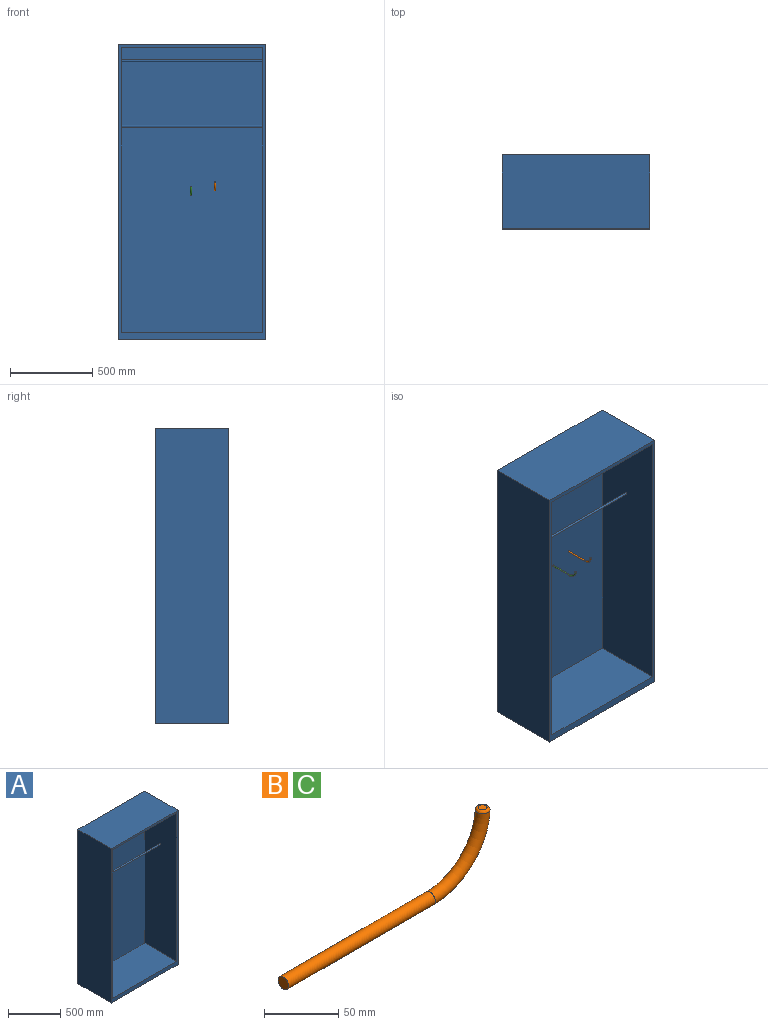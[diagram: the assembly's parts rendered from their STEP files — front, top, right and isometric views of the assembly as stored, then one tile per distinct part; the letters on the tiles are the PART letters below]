
ASSEMBLY  parts=3 mates=1
PART A: 13 faces, bbox 900x450x1800 mm
  f0: plane 1800x900mm, normal (0,-1,0), area 122688mm2, adj f1,f2,f3,f4,f6,f7,f8,f9
  f1: plane 1800x450mm, normal (-1,0,0), area 810000mm2, adj f0,f2,f4,f5
  f2: plane 900x450mm, normal (0,0,-1), area 405000mm2, adj f0,f1,f3,f5
  f3: plane 1800x450mm, normal (1,0,0), area 810000mm2, adj f0,f2,f4,f5
  f4: plane 900x450mm, normal (0,0,1), area 405000mm2, adj f0,f1,f3,f5
  f5: plane 1800x900mm, normal (0,1,0), area 1620000mm2, adj f1,f2,f3,f4
  f6: plane 1733x428mm, normal (1,0,0), area 741497.8mm2, adj f0,f7,f9,f10,f11,f12
  f7: plane 864x428mm, normal (0,0,1), area 369792mm2, adj f0,f6,f8,f10
  f8: plane 1733x428mm, normal (-1,0,0), area 741497.8mm2, adj f0,f7,f9,f10,f11,f12
  f9: plane 864x428mm, normal (0,0,-1), area 369792mm2, adj f0,f6,f8,f10
  f10: plane 1733x864mm, normal (0,-1,0), area 1497312mm2, adj f6,f7,f8,f9
  f11: cylinder r=6mm len=864mm, axis (1,0,0), area 32572mm2, adj f6,f8
  f12: cylinder r=6mm len=864mm, axis (1,0,0), area 32572mm2, adj f6,f8
PART B: 5 faces, bbox 199.5x10x59.5 mm
  f0: plane 10x10mm, normal (-1,0,0), area 78.5mm2, adj f2
  f1: plane 6.01x6mm, normal (0,0,1), area 28.3mm2, adj f4
  f2: cylinder r=5mm len=140mm, axis (1,0,0), area 4398.2mm2, adj f0,f3
  f3: torus R=50mm, axis (0,-1,0), area 2404.2mm2, adj f2,f4
  f4: bspline ~10.09x10.01mm, area 84.3mm2, adj f1,f3
PART C: same geometry as B
PLACE A t=(-1077.86,-489.46,-619)mm
PLACE B rot(axis=(0,0,-1),90deg) t=(-487.86,-61.46,292.5)mm
PLACE C rot(axis=(0,0,-1),90deg) t=(-633.98,-75.33,267.1)mm
MATE planar A.f10 <-> B.f2  axis (0,-1,0) through (-627.86,-61.46,292.5)mm
